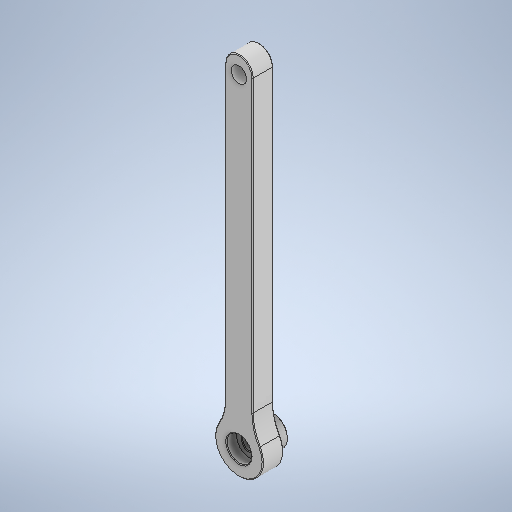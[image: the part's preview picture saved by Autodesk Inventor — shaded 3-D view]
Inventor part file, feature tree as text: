
AUTODESK INVENTOR PART (.ipt)
format: ipt  version: 2025.1 (Build 291241000, 241)  size: 334,336 bytes
history: native  units: mm
features: extrude x5, sketch x4, fillet x4
ambient origin geometry x8: Origin, YZ Plane, XZ Plane, XY Plane, X Axis, Y Axis, Z Axis, Center Point
bodies: Volumenkörper1 (feature_tree)
feature tree (13):
  sketch  "Skizze1"  dims[d2=14.0mm d4=15.0mm]
  extrude  "Extrusion1"  Depth=15.0mm
  extrude  "Extrusion5"  Depth=6.0mm TaperAngle=0.0deg
  fillet  "Rundung3"  [1 undecoded]
  fillet  "Rundung4"  Radius=100.0mm
  extrude  "Extrusion6"  Depth=4.0mm
  extrude  "Extrusion7"  Depth=4.0mm TaperAngle=0.0deg
  fillet  "Rundung5"  Radius=0.2mm
  fillet  "Rundung6"  Radius=0.2mm
  extrude  "Extrusion8"  Depth=10.0mm
  sketch  "Skizze8"  dims[d5=15.0mm d6=6.0mm d7=0.0mm d10=0.0mm d11=100.0mm]
  sketch  "Skizze10"  dims[d33=4.0mm d34=4.0mm]
  sketch  "Skizze11"  dims[d36=8.8mm d37=4.0mm d38=0.0mm d39=0.2mm d40=0.2mm d41=7.3mm d42=3.0mm d43=0.0mm d44=4.2mm d45=3.0mm d46=0.0mm d47=0.2mm d48=0.2mm d49=95.0mm d50=4.0mm d51=4.5mm d52=10.0mm d53=0.0mm]
note: 1 required parameter value undecoded (feature->parameter linkage not recoverable at this tier; creation-order binding heuristic only, values carry confidence <= 0.55)
